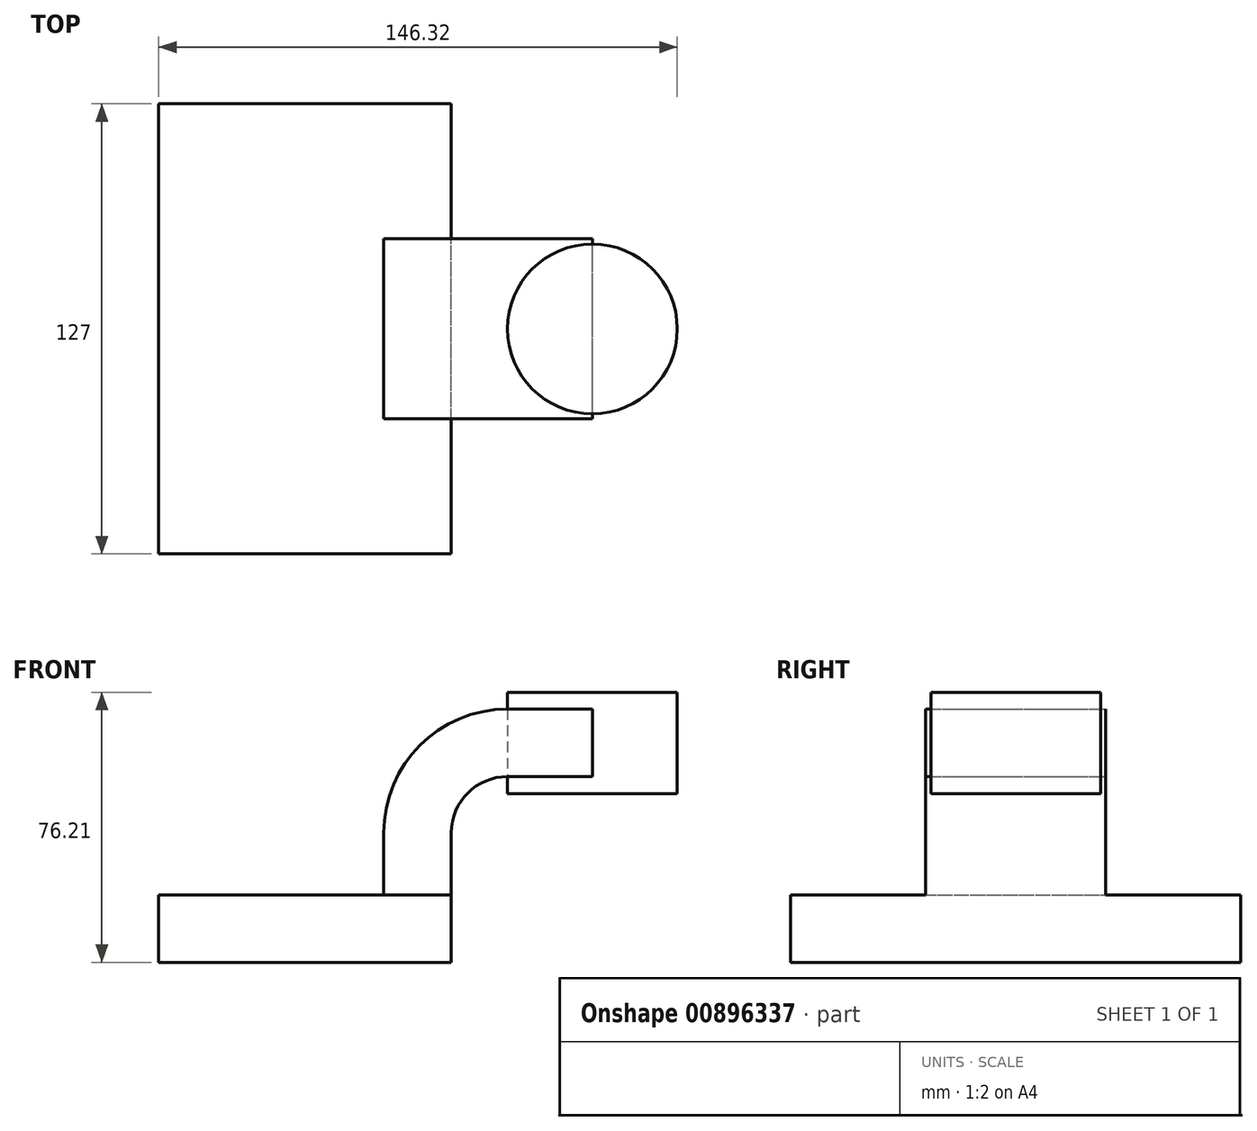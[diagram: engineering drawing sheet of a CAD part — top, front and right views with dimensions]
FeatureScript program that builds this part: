
annotation { "Feature Type Name" : "Feature", "Feature Type Description" : "" }
export const myFeature = defineFeature(function(context is Context, id is Id, definition is map)
    precondition{}
    {
        {
            var Q0;
            Q0=qCreatedBy(makeId("Front.planeOp"),FACE);
            var sketch = newSketch(context, id + "F0", { "sketchPlane" : qUnion([Q0])});
            skLineSegment(sketch, "E0.bottom", {"start": v(41.28, -9.52) * mm, "end": v(-41.28, -9.53) * mm});
            skLineSegment(sketch, "E0.top", {"start": v(41.28, 9.53) * mm, "end": v(-41.28, 9.53) * mm});
            skLineSegment(sketch, "E0.left", {"start": v(41.28, -9.52) * mm, "end": v(41.28, 9.53) * mm});
            skLineSegment(sketch, "E0.right", {"start": v(-41.28, -9.53) * mm, "end": v(-41.28, 9.53) * mm});
            skPoint(sketch, "E0.middle", {"position": v(0, 0) * mm});
            skLineSegment(sketch, "E1.bottom", {"start": v(105.04, 38.1) * mm, "end": v(57.15, 38.1) * mm});
            skLineSegment(sketch, "E1.top", {"start": v(105.04, 66.68) * mm, "end": v(54.24, 66.68) * mm});
            skLineSegment(sketch, "E1.left", {"start": v(105.04, 38.1) * mm, "end": v(105.04, 66.68) * mm});
            skPoint(sketch, "E1.middle", {"position": v(79.64, 52.39) * mm});
            skLineSegment(sketch, "E2", {"start": v(41.28, 9.53) * mm, "end": v(41.28, 27) * mm});
            skArc(sketch, "E3", {"start": v(41.27, 27) * mm, "mid": v(45.92, 38.23) * mm, "end": v(57.15, 42.88) * mm});
            skLineSegment(sketch, "E4", {"start": v(57.15, 42.88) * mm, "end": v(81.1, 42.88) * mm});
            skArc(sketch, "E5.0", {"start": v(22.23, 27) * mm, "mid": v(32.45, 51.7) * mm, "end": v(57.15, 61.93) * mm});
            skLineSegment(sketch, "E5.1", {"start": v(22.22, 9.53) * mm, "end": v(22.22, 27) * mm});
            skFitSpline(sketch, "E6", {"points": [v(-41.28, 9.52) * mm, v(54.24, 66.67) * mm], "startDerivative": vector(1.6, 57.08) * mm, "endDerivative": vector(103.23, -0.3) * mm});
            skLineSegment(sketch, "E7", {"start": v(57.15, 42.88) * mm, "end": v(57.15, 38.1) * mm});
            skLineSegment(sketch, "E8", {"start": v(57.15, 38.1) * mm, "end": v(57.15, 66.68) * mm});
            skPoint(sketch, "E9.orphan", {"position": v(54.24, 38.1) * mm});
            skLineSegment(sketch, "E10", {"start": v(81.1, 38.1) * mm, "end": v(81.1, 66.68) * mm});
            skLineSegment(sketch, "E11", {"start": v(57.15, 61.93) * mm, "end": v(81.1, 61.93) * mm});
            skPoint(sketch, "E12.orphan", {"position": v(85.73, 42.88) * mm});
            skSolve(sketch);
        }
        {
            var Q0;
            Q0=makeQuery(id+"F0.imprint","IMPRINT",FACE,{"disambiguationData":[TD([[makeQuery(id+"F0.imprint","IMPRINT",EDGE,{"derivedFrom":sQuery(id+"F0.wireOp",EDGE,"E0.bottom")}),-1.0]])]});
            extrude(context, id + "F1", {"entities" : qUnion([Q0]), "endBound" : BoundingType.SYMMETRIC, "depth" : 127 * mm, "offsetDistance" : 25.4 * mm});
        }
        {
            var Q0;
            {var subQ2=sQuery(id+"F0.wireOp",EDGE,"E2");Q0=makeQuery(id+"F0.imprint","IMPRINT",FACE,{"disambiguationData":[TD([[makeQuery(id+"F0.imprint","IMPRINT",EDGE,{"derivedFrom":subQ2}),1.0]])]});}
            var Q1;
            {var subQ0=sQuery(id+"F0.wireOp",EDGE,"E4");Q1=makeQuery(id+"F0.imprint","IMPRINT",FACE,{"disambiguationData":[TD([[makeQuery(id+"F0.imprint","IMPRINT",EDGE,{"derivedFrom":subQ0}),1.0]])]});}
            extrude(context, id + "F2", {"entities" : qUnion([Q0, Q1]), "operationType" : NewBodyOperationType.ADD, "endBound" : BoundingType.SYMMETRIC, "depth" : 50.8 * mm, "offsetDistance" : 25.4 * mm});
        }
        {
            var Q0;
            {var subQ1=sQuery(id+"F0.wireOp",EDGE,"E5.0");Q0=makeQuery(id+"F0.imprint","IMPRINT",FACE,{"disambiguationData":[TD([[makeQuery(id+"F0.imprint","IMPRINT",EDGE,{"derivedFrom":subQ1}),1.0]])]});}
            extrude(context, id + "F3", {"entities" : qUnion([Q0]), "operationType" : NewBodyOperationType.ADD, "endBound" : BoundingType.SYMMETRIC, "depth" : 15.88 * mm, "offsetDistance" : 25.4 * mm});
        }
        {
            var Q0;
            {var subQ0=sQuery(id+"F0.wireOp",EDGE,"E1.left");Q0=makeQuery(id+"F0.imprint","IMPRINT",FACE,{"disambiguationData":[TD([[makeQuery(id+"F0.imprint","IMPRINT",EDGE,{"derivedFrom":subQ0}),1.0]])]});}
            var Q1;
            Q1=sQuery(id+"F0.wireOp",EDGE,"E10");
            revolve(context, id + "F4", {"surfaceOperationType" : NewSurfaceOperationType.NEW, "entities" : qUnion([Q0]), "axis" : qUnion([Q1]), "revolveType" : RevolveType.FULL});
        }
    });
